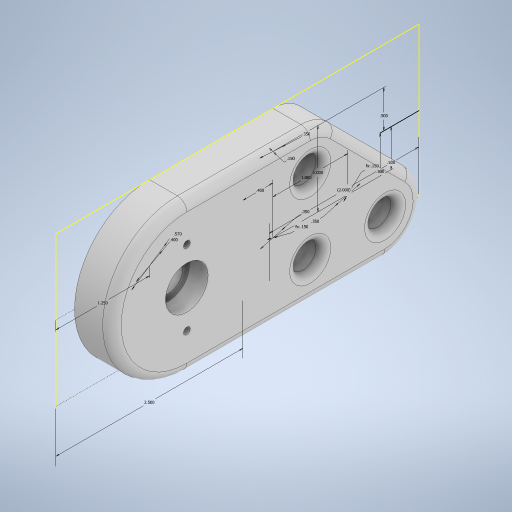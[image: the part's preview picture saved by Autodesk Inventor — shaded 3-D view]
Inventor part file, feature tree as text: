
AUTODESK INVENTOR PART (.ipt)
format: ipt  version: 2024 (Build 280153000, 153)  size: 828,928 bytes
history: native  units: in
note: dims shown in document units (in); Inventor stores cm internally (conversion verified against a paired STEP export)
features: extrude x13, sketch x9, fillet x8, projected_geometry x2, chamfer x1
ambient origin geometry x8: Origin, YZ Plane, XZ Plane, XY Plane, X Axis, Y Axis, Z Axis, Center Point
bodies: Solid1 (feature_tree)
feature tree (33):
  extrude  "Extrusion1"  Depth=0.5in
  sketch  "Sketch2"  dims[d4=2.5in d6=5.5in]
  extrude  "Extrusion4"  Depth=5.5in
  extrude  "Extrusion5"  Depth=2.0in
  chamfer  "Chamfer1"  Distance=2.0in
  fillet  "Fillet3"  Radius=2.0in
  fillet  "Fillet8"  Radius=2.5in
  sketch  "Sketch6"  dims[d13=1.25in d14=2.0in d15=0.0in d16=2.0in d17=2.5in]
  extrude  "Extrusion11"  Depth=0.15in
  extrude  "Extrusion12"  Depth=0.15in
  extrude  "Extrusion13"  Depth=0.3in
  extrude  "Extrusion14"  Depth=1.0in
  extrude  "Extrusion16"  Depth=1.0in
  fillet  "Fillet13"  Radius=0.4in
  fillet  "Fillet14"  [1 undecoded]
  sketch  "Sketch3"  dims[d7=2.0in d8=1.04in]
  extrude  "Extrusion6"  Depth=0.3in TaperAngle=0.0deg
  extrude  "Extrusion7"  Depth=0.5in
  fillet  "Fillet4"  Radius=0.5in
  extrude  "Extrusion8"  Depth=0.5in
  extrude  "Extrusion9"  Depth=1.0in TaperAngle=45.0deg
  extrude  "Extrusion10"  Depth=0.5in
  fillet  "Fillet5"  Radius=1.25in
  fillet  "Fillet6"  Radius=0.09in
  fillet  "Fillet7"  Radius=0.35in
  sketch  "Sketch1"  dims[d1=0.35in d3=0.5in]
  sketch  "Sketch4"  dims[d9=0.5in]
  sketch  "Sketch5"  dims[d10=4.0in]
  projected_geometry  "Projected Loop1"
  sketch  "Sketch7"  dims[d32=0.15in d34=0.15in]
  sketch  "Sketch8"  dims[d36=0.15in d38=0.35in]
  sketch  "Sketch9"  dims[d39=0.35in d40=0.35in d41=1.0in d42=1.0in d43=0.4in d44=0.0in d45=0.0in d46=0.3in d47=0.0in d49=0.5in d50=0.5in d51=0.5in d52=1.0in d53=0.125in d54=45.0deg d55=0.5in d56=1.25in d57=0.09in d58=0.35in d59=0.09in d60=0.35in d61=0.09in d62=0.3in d63=0.09in d64=0.3in d65=0.25in d66=0.25in d67=0.25in d68=0.25in d69=0.25in d70=0.0in d71=0.0in d72=0.35in d73=0.0in d74=0.05in d75=0.35in d76=0.0in d77=1.1in d78=1.5in d79=1.0in d80=0.0in d81=0.0in d82=0.0in d83=0.15in d84=0.15in d85=0.1in d86=0.1in d87=1.25in d88=0.57in d89=0.4in d90=0.25in d91=0.0in d92=0.0in d93=0.0in d95=0.5in d96=0.5in d97=0.09in d98=0.09in d99=0.1in d100=0.0in d101=0.0in d102=0.0in d108=0.5in d109=0.0in d110=0.0in d112=0.125in d113=0.3in]
  projected_geometry  "Projected Loop2"
note: 1 required parameter value undecoded (feature->parameter linkage not recoverable at this tier; creation-order binding heuristic only, values carry confidence <= 0.55)
